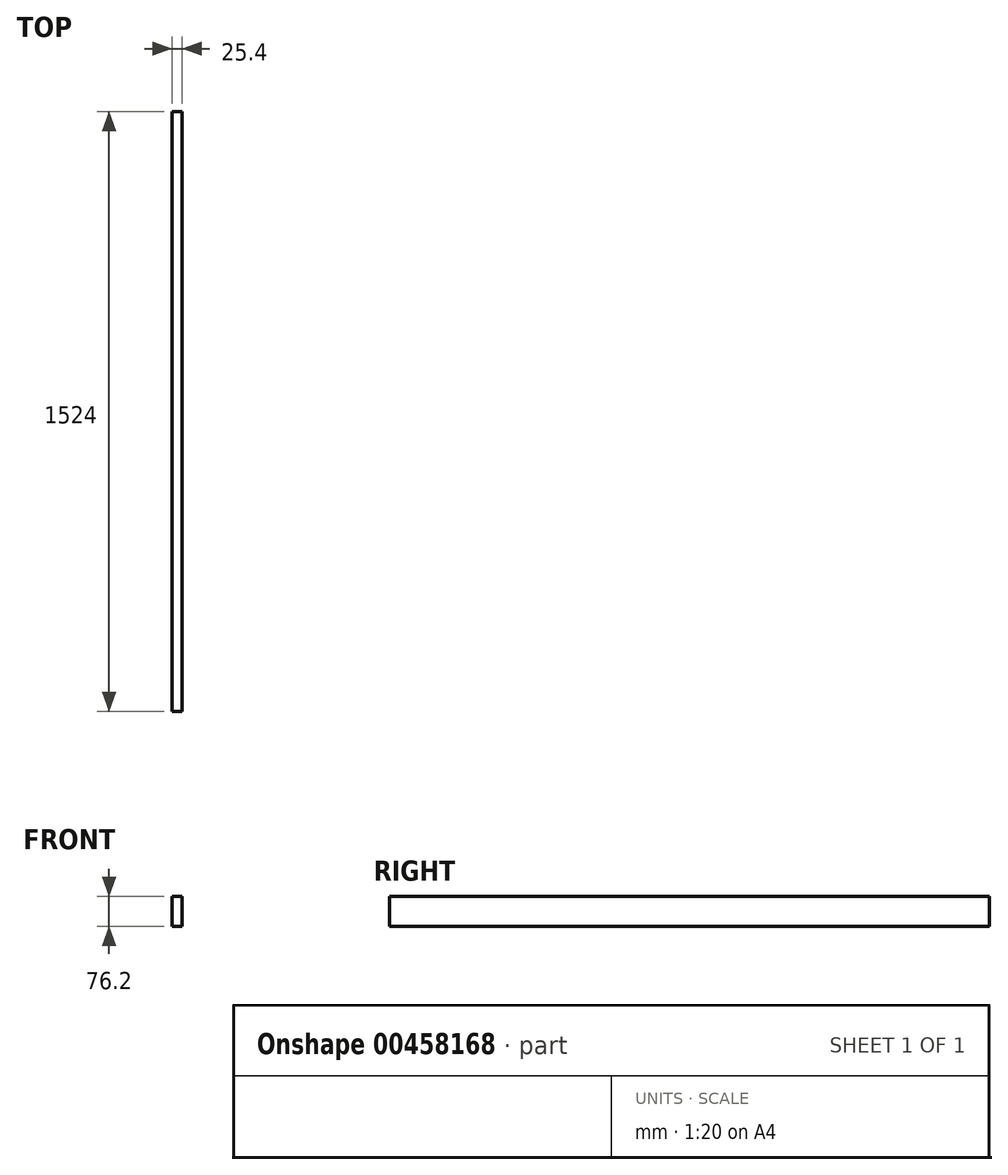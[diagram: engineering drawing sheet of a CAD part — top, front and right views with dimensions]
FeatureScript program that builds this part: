
annotation { "Feature Type Name" : "Feature", "Feature Type Description" : "" }
export const myFeature = defineFeature(function(context is Context, id is Id, definition is map)
    precondition{}
    {
        {
            var Q0;
            Q0=qCreatedBy(makeId("Front.planeOp"),FACE);
            var sketch = newSketch(context, id + "F0", { "sketchPlane" : qUnion([Q0])});
            skLineSegment(sketch, "E0.bottom", {"start": v(-10.07, 46.56) * mm, "end": v(15.33, 46.56) * mm});
            skLineSegment(sketch, "E0.top", {"start": v(-10.07, -29.64) * mm, "end": v(15.33, -29.64) * mm});
            skLineSegment(sketch, "E0.left", {"start": v(-10.07, 46.56) * mm, "end": v(-10.07, -29.64) * mm});
            skLineSegment(sketch, "E0.right", {"start": v(15.33, 46.56) * mm, "end": v(15.33, -29.64) * mm});
            skSolve(sketch);
        }
        {
            var Q0;
            Q0 = qSketchRegion(id + "F0", true);
            extrude(context, id + "F1", {"entities" : qUnion([Q0]), "oppositeDirection" : true, "depth" : 1524 * mm});
        }
    });
